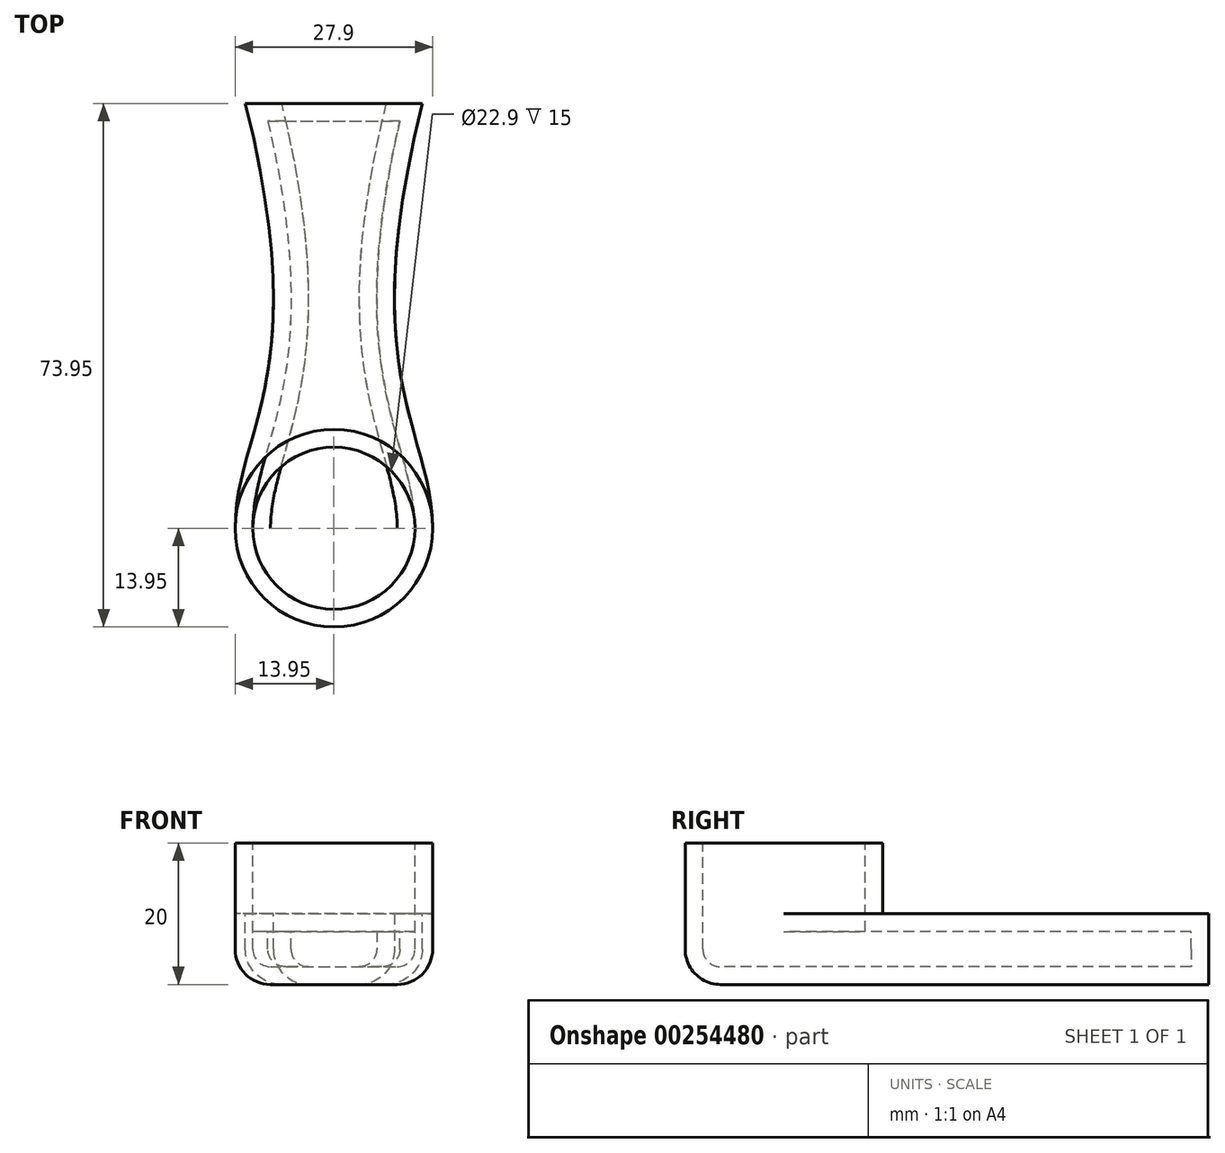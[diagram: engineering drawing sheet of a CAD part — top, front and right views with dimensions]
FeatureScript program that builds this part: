
annotation { "Feature Type Name" : "Feature", "Feature Type Description" : "" }
export const myFeature = defineFeature(function(context is Context, id is Id, definition is map)
    precondition{}
    {
        {
            var Q0;
            Q0=qCreatedBy(makeId("Top.planeOp"),FACE);
            var sketch = newSketch(context, id + "F0", { "sketchPlane" : qUnion([Q0])});
            skLineSegment(sketch, "E0.bottom", {"start": v(-12.5, 0) * mm, "end": v(12.5, 0) * mm});
            skCircle(sketch, "E1", {"center": v(0, -60) * mm, "radius": 13.95 * mm});
            skPoint(sketch, "E2", {"position": v(0, 0) * mm});
            skFitSpline(sketch, "E3", {"points": [v(-12.5, 0) * mm, v(-13.95, -60) * mm], "startDerivative": vector(29, -115.87) * mm, "endDerivative": vector(0, -41) * mm});
            skFitSpline(sketch, "E4.MirrorCS", {"points": [v(12.5, 0) * mm, v(13.95, -60) * mm], "startDerivative": vector(-29, -115.87) * mm, "endDerivative": vector(0, -41) * mm});
            skLineSegment(sketch, "E5", {"start": v(-13.95, -60) * mm, "end": v(13.95, -60) * mm});
            skSolve(sketch);
        }
        {
            var Q0;
            Q0=makeQuery(id+"F0.imprint","IMPRINT",FACE,{"disambiguationData":[TD([[makeQuery(id+"F0.imprint","IMPRINT",EDGE,{"derivedFrom":sQuery(id+"F0.wireOp",EDGE,"E0.bottom")}),-1.0]])]});
            var Q1;
            {var subQ0=sQuery(id+"F0.wireOp",EDGE,"E5");Q1=makeQuery(id+"F0.imprint","IMPRINT",FACE,{"disambiguationData":[TD([[makeQuery(id+"F0.imprint","IMPRINT",EDGE,{"derivedFrom":subQ0}),1.0]])]});}
            var Q2;
            {var subQ0=sQuery(id+"F0.wireOp",EDGE,"E5");Q2=makeQuery(id+"F0.imprint","IMPRINT",FACE,{"disambiguationData":[TD([[makeQuery(id+"F0.imprint","IMPRINT",EDGE,{"derivedFrom":subQ0}),-1.0]])]});}
            extrude(context, id + "F1", {"entities" : qUnion([Q0, Q1, Q2]), "oppositeDirection" : true, "depth" : 20 * mm});
        }
        {
            var Q0;
            Q0=makeQuery(id+"F0.imprint","IMPRINT",FACE,{"disambiguationData":[TD([[makeQuery(id+"F0.imprint","IMPRINT",EDGE,{"derivedFrom":sQuery(id+"F0.wireOp",EDGE,"E0.bottom")}),-1.0]])]});
            extrude(context, id + "F2", {"entities" : qUnion([Q0]), "operationType" : NewBodyOperationType.REMOVE, "oppositeDirection" : true, "depth" : 10 * mm});
        }
        {
            var Q0;
            Q0=makeQuery(id+"F2.boolean.opBoolean","COPY",EDGE,{"derivedFrom":makeQuery(id+"F2.opExtrude","CAP_EDGE",EDGE,{"disambiguationData":[OSD([sQuery(id+"F0.wireOp",EDGE,"E4.MirrorCS")])],"isStart":false})});
            var Q1;
            Q1=makeQuery(id+"F1.opExtrude","CAP_EDGE",EDGE,{"disambiguationData":[OSD([sQuery(id+"F0.wireOp",EDGE,"E4.MirrorCS")])],"isStart":false});
            var Q2;
            Q2=makeQuery(id+"F2.boolean.opBoolean","COPY",EDGE,{"derivedFrom":makeQuery(id+"F2.opExtrude","CAP_EDGE",EDGE,{"disambiguationData":[OSD([sQuery(id+"F0.wireOp",EDGE,"E3")])],"isStart":false})});
            var Q3;
            Q3=makeQuery(id+"F1.opExtrude","CAP_EDGE",EDGE,{"disambiguationData":[OSD([sQuery(id+"F0.wireOp",EDGE,"E3")])],"isStart":false});
            fillet(context, id + "F3", {"entities" : qUnion([Q0, Q1, Q2, Q3]), "radius" : 5 * mm, "tangentPropagation" : true, "allowEdgeOverflow" : false});
        }
        {
            var Q0;
            Q0=makeQuery(id+"F1.opExtrude","CAP_FACE",FACE,{"disambiguationData":[OSD([sQuery(id+"F0.wireOp",EDGE,"E0.bottom"),sQuery(id+"F0.wireOp",EDGE,"E1"),sQuery(id+"F0.wireOp",EDGE,"E3"),sQuery(id+"F0.wireOp",EDGE,"E4.MirrorCS")])],"isStart":true});
            shell(context, id + "F4", {"entities" : qUnion([Q0]), "thickness" : 2.5 * mm});
        }
    });
